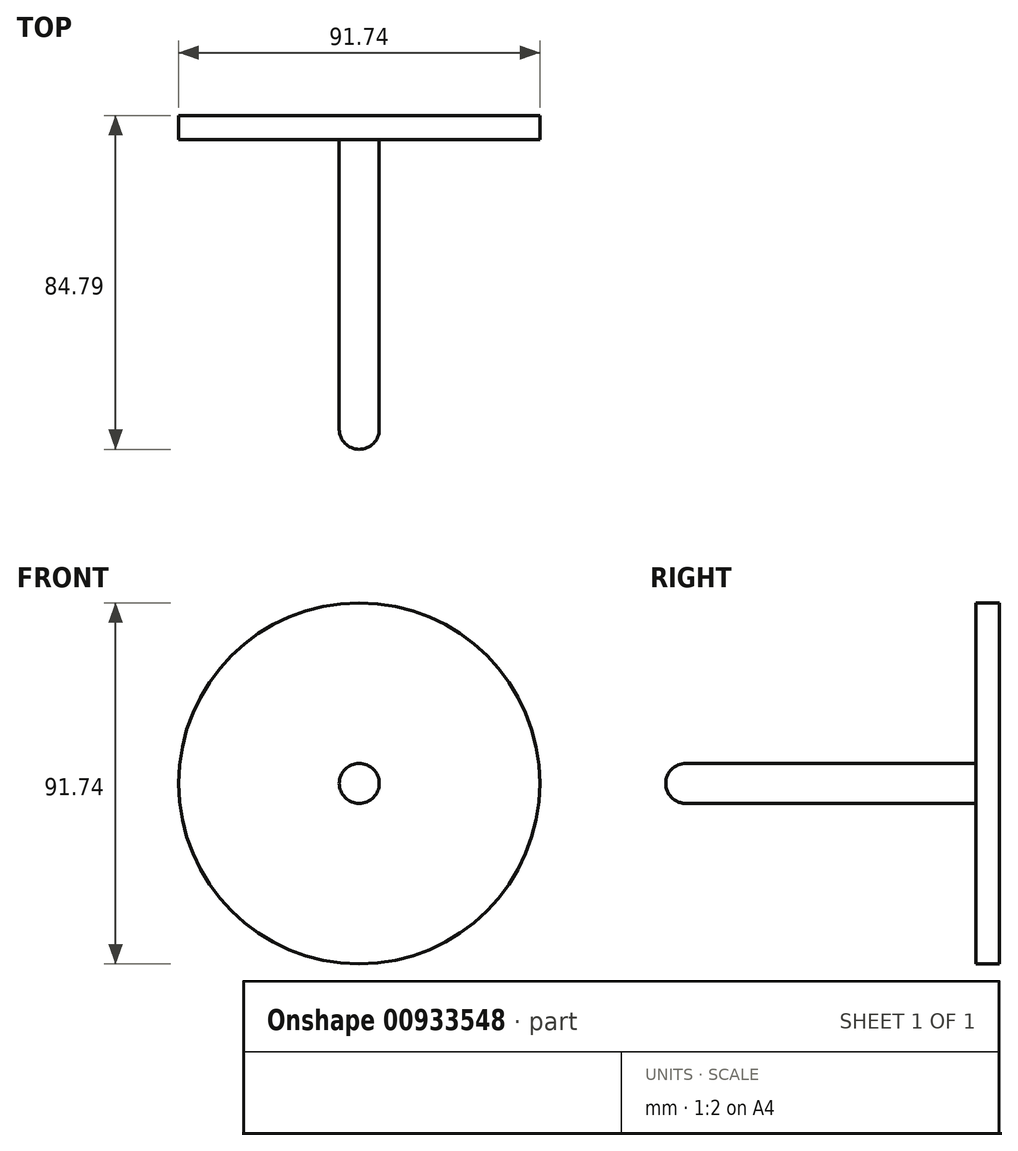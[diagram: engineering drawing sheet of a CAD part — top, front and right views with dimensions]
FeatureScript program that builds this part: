
annotation { "Feature Type Name" : "Feature", "Feature Type Description" : "" }
export const myFeature = defineFeature(function(context is Context, id is Id, definition is map)
    precondition{}
    {
        {
            var Q0;
            Q0=qCreatedBy(makeId("Front.planeOp"),FACE);
            var sketch = newSketch(context, id + "F0", { "sketchPlane" : qUnion([Q0])});
            skCircle(sketch, "E0", {"center": v(0, 0) * mm, "radius": 45.87 * mm});
            skSolve(sketch);
        }
        {
            var Q0;
            Q0 = qSketchRegion(id + "F0", true);
            extrude(context, id + "F1", {"entities" : qUnion([Q0]), "depth" : 6.05 * mm, "offsetDistance" : 25.4 * mm});
        }
        {
            var Q0;
            Q0=makeQuery(id+"F1.opExtrude","CAP_FACE",FACE,{"disambiguationData":[OSD([sQuery(id+"F0.wireOp",EDGE,"E0")])],"isStart":false});
            var sketch = newSketch(context, id + "F2", { "sketchPlane" : qUnion([Q0])});
            skCircle(sketch, "E1.0.0", {"center": v(0, 0) * mm, "radius": 45.87 * mm});
            skCircle(sketch, "E2", {"center": v(0, 0) * mm, "radius": 5.08 * mm});
            skSolve(sketch);
        }
        {
            var Q0;
            Q0=makeQuery(id+"F2.imprint","IMPRINT",FACE,{"disambiguationData":[TD([[makeQuery(id+"F2.imprint","IMPRINT",EDGE,{"derivedFrom":sQuery(id+"F2.wireOp",EDGE,"E2")}),1.0]])]});
            extrude(context, id + "F3", {"entities" : qUnion([Q0]), "operationType" : NewBodyOperationType.ADD, "depth" : 78.74 * mm, "offsetDistance" : 25.4 * mm});
        }
        {
            var Q0;
            Q0=makeQuery(id+"F3.opExtrude","CAP_EDGE",EDGE,{"disambiguationData":[OSD([sQuery(id+"F2.wireOp",EDGE,"E2")])],"isStart":false});
            fillet(context, id + "F4", {"entities" : qUnion([Q0]), "radius" : 5.08 * mm, "tangentPropagation" : true, "allowEdgeOverflow" : false});
        }
    });
